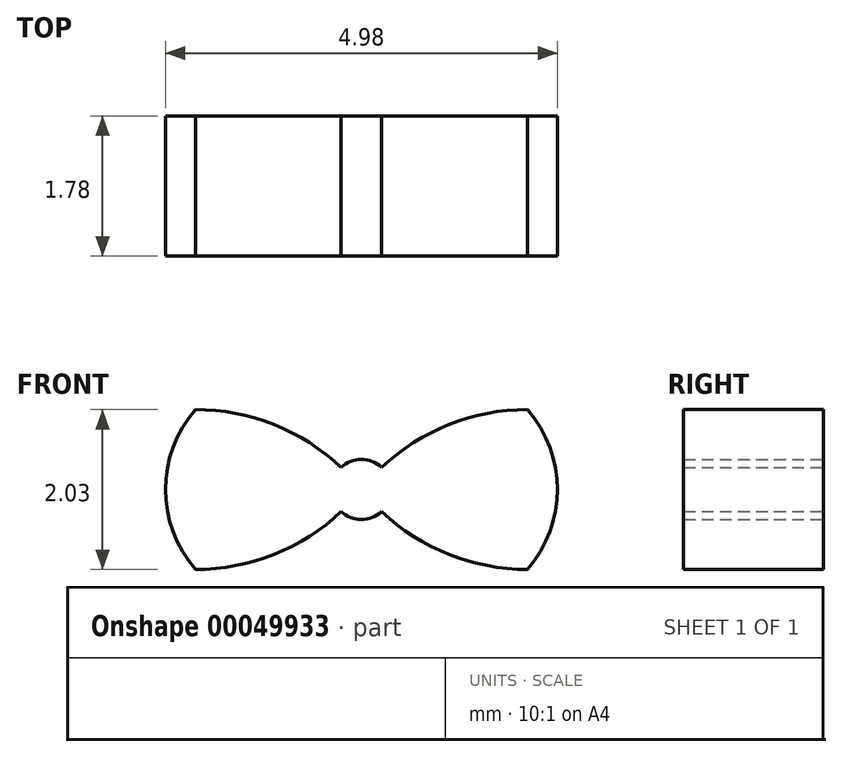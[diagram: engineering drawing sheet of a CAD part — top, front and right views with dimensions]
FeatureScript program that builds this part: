
annotation { "Feature Type Name" : "Feature", "Feature Type Description" : "" }
export const myFeature = defineFeature(function(context is Context, id is Id, definition is map)
    precondition{}
    {
        {
            var Q0;
            Q0=qCreatedBy(makeId("Front.planeOp"),FACE);
            var sketch = newSketch(context, id + "F0", { "sketchPlane" : qUnion([Q0])});
            skLineSegment(sketch, "E0", {"start": v(0, 0) * mm, "end": v(2.1, 0) * mm, "construction": true});
            skLineSegment(sketch, "E1", {"start": v(2.1, 0) * mm, "end": v(2.1, 2.03) * mm, "construction": true});
            skLineSegment(sketch, "E2", {"start": v(2.1, 2.03) * mm, "end": v(0, 2.03) * mm, "construction": true});
            skLineSegment(sketch, "E3", {"start": v(0, 2.03) * mm, "end": v(0, 0) * mm, "construction": true});
            skLineSegment(sketch, "E4", {"start": v(0, 0) * mm, "end": v(-2.1, 0) * mm, "construction": true});
            skLineSegment(sketch, "E5", {"start": v(-2.1, 0) * mm, "end": v(-2.1, 2.03) * mm, "construction": true});
            skLineSegment(sketch, "E6", {"start": v(-2.1, 2.03) * mm, "end": v(0, 2.03) * mm, "construction": true});
            skLineSegment(sketch, "E7", {"start": v(-2.1, 2.03) * mm, "end": v(-2.1, 0) * mm});
            skLineSegment(sketch, "E8", {"start": v(2.1, 2.03) * mm, "end": v(2.1, 0) * mm});
            skCircle(sketch, "E9", {"center": v(0, 1.02) * mm, "radius": 0.38 * mm});
            skArc(sketch, "E10", {"start": v(0, 1.02) * mm, "mid": v(-0.94, 1.76) * mm, "end": v(-2.1, 2.03) * mm});
            skArc(sketch, "E11", {"start": v(2.1, 2.03) * mm, "mid": v(0.94, 1.76) * mm, "end": v(0, 1.02) * mm});
            skArc(sketch, "E12", {"start": v(0, 1.02) * mm, "mid": v(0.94, 0.27) * mm, "end": v(2.1, 0) * mm});
            skArc(sketch, "E13", {"start": v(-2.1, 0) * mm, "mid": v(-0.94, 0.27) * mm, "end": v(0, 1.02) * mm});
            skLineSegment(sketch, "E14", {"start": v(-2.1, 1.02) * mm, "end": v(-2.49, 1.02) * mm});
            skLineSegment(sketch, "E15", {"start": v(2.1, 1.02) * mm, "end": v(2.49, 1.02) * mm});
            skArc(sketch, "E16", {"start": v(-2.1, 2.03) * mm, "mid": v(-2.49, 1.02) * mm, "end": v(-2.1, 0) * mm});
            skArc(sketch, "E17", {"start": v(2.1, 0) * mm, "mid": v(2.49, 1.02) * mm, "end": v(2.1, 2.03) * mm});
            skLineSegment(sketch, "E18", {"start": v(-2.1, 2.03) * mm, "end": v(2.1, 2.03) * mm, "construction": true});
            skSolve(sketch);
        }
        {
            var Q0;
            Q0 = qSketchRegion(id + "F0", true);
            extrude(context, id + "F1", {"entities" : qUnion([Q0]), "depth" : 1.78 * mm});
        }
    });
